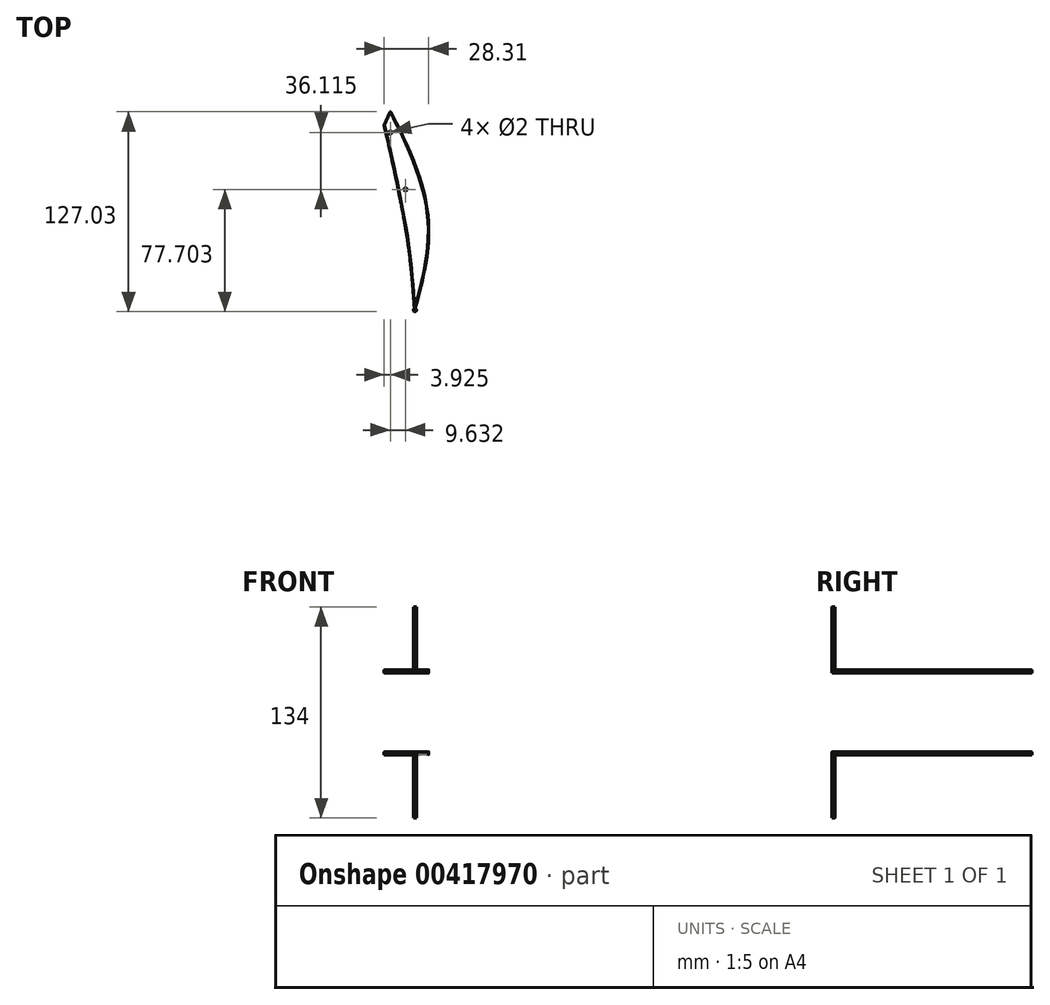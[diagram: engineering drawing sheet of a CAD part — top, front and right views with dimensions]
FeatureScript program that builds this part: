
annotation { "Feature Type Name" : "Feature", "Feature Type Description" : "" }
export const myFeature = defineFeature(function(context is Context, id is Id, definition is map)
    precondition{}
    {
        {
            var Q0;
            Q0=qCreatedBy(makeId("Top.planeOp"),FACE);
            var sketch = newSketch(context, id + "F0", { "sketchPlane" : qUnion([Q0])});
            skCircle(sketch, "E0", {"center": v(0, 0) * mm, "radius": 1 * mm});
            skSolve(sketch);
        }
        {
            var Q0;
            Q0 = qSketchRegion(id + "F0", true);
            extrude(context, id + "F1", {"entities" : qUnion([Q0]), "oppositeDirection" : true, "depth" : 42 * mm});
        }
        {
            var Q0;
            Q0=qCreatedBy(makeId("Top.planeOp"),FACE);
            var sketch = newSketch(context, id + "F2", { "sketchPlane" : qUnion([Q0])});
            skCircle(sketch, "E1.0", {"center": v(0, 0) * mm, "radius": 1 * mm});
            skFitSpline(sketch, "E2", {"points": [v(-0.23, 0.97) * mm, v(-7.5, 61.32) * mm, v(-19.51, 117.28) * mm], "startDerivative": vector(-11.83, 161.26) * mm, "endDerivative": vector(-15.76, 63.42) * mm});
            skLineSegment(sketch, "E3", {"start": v(-19.51, 117.28) * mm, "end": v(-15.63, 126.3) * mm});
            skFitSpline(sketch, "E4", {"points": [v(0.23, 0.97) * mm, v(8.32, 59.98) * mm, v(-15.63, 126.3) * mm], "startDerivative": vector(32.08, 121.42) * mm, "endDerivative": vector(-62.93, 119.77) * mm});
            skSolve(sketch);
        }
        {
            var Q0;
            {var subQ0=sQuery(id+"F2.wireOp",EDGE,"E2");Q0=makeQuery(id+"F2.imprint","IMPRINT",FACE,{"disambiguationData":[TD([[makeQuery(id+"F2.imprint","IMPRINT",EDGE,{"derivedFrom":subQ0}),-1.0]])]});}
            extrude(context, id + "F3", {"entities" : qUnion([Q0]), "operationType" : NewBodyOperationType.ADD, "oppositeDirection" : true, "depth" : 2 * mm});
        }
        {
            var Q0;
            Q0=makeQuery(id+"F3.opExtrude","CAP_EDGE",EDGE,{"disambiguationData":[OSD([sQuery(id+"F2.wireOp",EDGE,"E4")])],"isStart":false});
            var Q1;
            Q1=makeQuery(id+"F3.opExtrude","CAP_EDGE",EDGE,{"disambiguationData":[OSD([sQuery(id+"F2.wireOp",EDGE,"E4")])],"isStart":true});
            var Q2;
            Q2=makeQuery(id+"F3.opExtrude","CAP_EDGE",EDGE,{"disambiguationData":[OSD([sQuery(id+"F2.wireOp",EDGE,"E2")])],"isStart":true});
            var Q3;
            Q3=makeQuery(id+"F3.opExtrude","CAP_EDGE",EDGE,{"disambiguationData":[OSD([sQuery(id+"F2.wireOp",EDGE,"E2")])],"isStart":false});
            var Q4;
            Q4=makeQuery(id+"F3.opExtrude","CAP_EDGE",EDGE,{"disambiguationData":[OSD([sQuery(id+"F2.wireOp",EDGE,"E3")])],"isStart":true});
            var Q5;
            Q5=makeQuery(id+"F3.opExtrude","SWEPT_EDGE",EDGE,{"disambiguationData":[OSD([sQuery(id+"F2.wireOp",EDGE,"E2"),sQuery(id+"F2.wireOp",EDGE,"E3")])]});
            var Q6;
            Q6=makeQuery(id+"F3.opExtrude","CAP_EDGE",EDGE,{"disambiguationData":[OSD([sQuery(id+"F2.wireOp",EDGE,"E3")])],"isStart":false});
            var Q7;
            Q7=makeQuery(id+"F3.opExtrude","SWEPT_EDGE",EDGE,{"disambiguationData":[OSD([sQuery(id+"F2.wireOp",EDGE,"E3"),sQuery(id+"F2.wireOp",EDGE,"E4")])]});
            fillet(context, id + "F4", {"entities" : qUnion([Q0, Q1, Q2, Q3, Q4, Q5, Q6, Q7]), "radius" : 0.2 * mm, "tangentPropagation" : true, "allowEdgeOverflow" : false});
        }
        {
            var Q0;
            Q0=qCreatedBy(makeId("Top.planeOp"),FACE);
            var sketch = newSketch(context, id + "F5", { "sketchPlane" : qUnion([Q0])});
            skCircle(sketch, "E5", {"center": v(-15.58, 112.82) * mm, "radius": 1 * mm});
            skCircle(sketch, "E6", {"center": v(-5.94, 76.7) * mm, "radius": 1 * mm});
            skSolve(sketch);
        }
        {
            var Q0;
            Q0 = qSketchRegion(id + "F5", true);
            extrude(context, id + "F6", {"entities" : qUnion([Q0]), "operationType" : NewBodyOperationType.REMOVE, "oppositeDirection" : true, "depth" : 25 * mm});
        }
        {
            var Q0;
            Q0=qCreatedBy(makeId("Top.planeOp"),FACE);
            cPlane(context, id + "F7", {"entities" : qUnion([Q0]), "cplaneType" : CPlaneType.OFFSET, "offset" : 25 * mm, "width" : 150 * mm, "height" : 150 * mm});
        }
        {
            var Q0;
            Q0=makeQuery(id+"F1.opExtrude","SWEPT_BODY",BODY,{"disambiguationData":[OSD([sQuery(id+"F0.wireOp",EDGE,"E0")])]});
            var Q1;
            Q1=qCreatedBy(id+"F7.planeOp",FACE);
            mirror(context, id + "F8", {"entities" : qUnion([Q0]), "mirrorPlane" : qUnion([Q1])});
        }
    });
